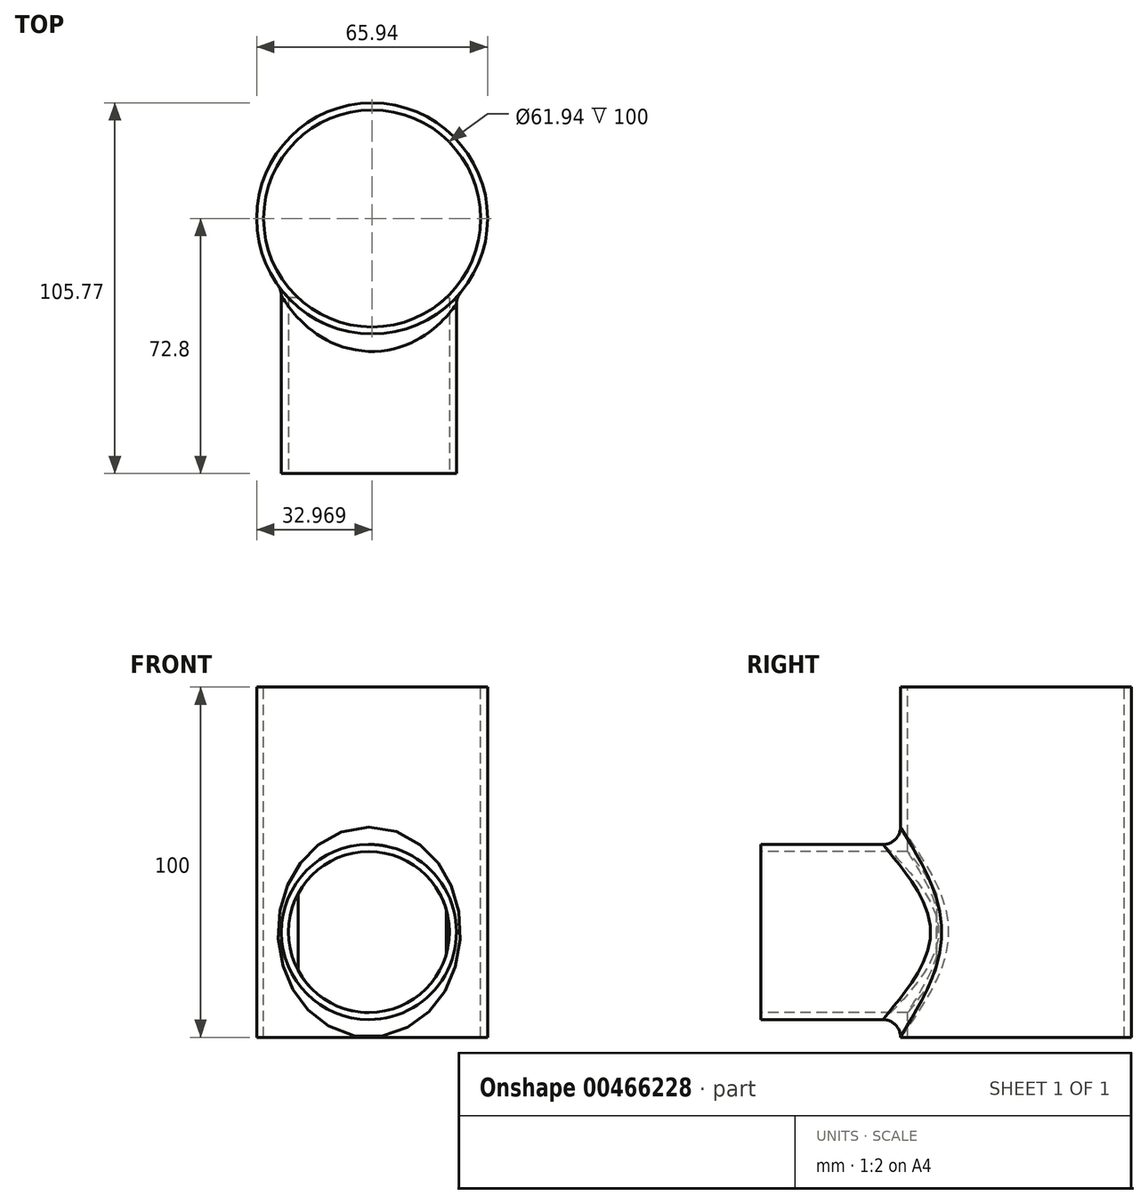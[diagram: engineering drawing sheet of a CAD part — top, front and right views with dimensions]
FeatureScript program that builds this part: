
annotation { "Feature Type Name" : "Feature", "Feature Type Description" : "" }
export const myFeature = defineFeature(function(context is Context, id is Id, definition is map)
    precondition{}
    {
        {
            var Q0;
            Q0=qCreatedBy(makeId("Top.planeOp"),FACE);
            var sketch = newSketch(context, id + "F0", { "sketchPlane" : qUnion([Q0])});
            skCircle(sketch, "E0", {"center": v(35.44, 0) * mm, "radius": 32.97 * mm});
            skSolve(sketch);
        }
        {
            var Q0;
            Q0=makeQuery(id+"F0.imprint","IMPRINT",FACE,{"disambiguationData":[TD([[makeQuery(id+"F0.imprint","IMPRINT",EDGE,{"derivedFrom":sQuery(id+"F0.wireOp",EDGE,"E0")}),1.0]])]});
            extrude(context, id + "F1", {"entities" : qUnion([Q0]), "depth" : 100 * mm, "offsetDistance" : 25 * mm});
        }
        {
            var Q0;
            Q0=makeQuery(id+"F1.opExtrude","CAP_FACE",FACE,{"disambiguationData":[OSD([sQuery(id+"F0.wireOp",EDGE,"E0")])],"isStart":false});
            var sketch = newSketch(context, id + "F2", { "sketchPlane" : qUnion([Q0])});
            skCircle(sketch, "E1.0", {"center": v(35.44, 0) * mm, "radius": 30.97 * mm});
            skSolve(sketch);
        }
        {
            var Q0;
            Q0=makeQuery(id+"F2.imprint","IMPRINT",FACE,{"disambiguationData":[TD([[makeQuery(id+"F2.imprint","IMPRINT",EDGE,{"derivedFrom":sQuery(id+"F2.wireOp",EDGE,"E1.0")}),1.0]])]});
            extrude(context, id + "F3", {"entities" : qUnion([Q0]), "operationType" : NewBodyOperationType.REMOVE, "oppositeDirection" : true, "depth" : 100 * mm, "offsetDistance" : 25 * mm});
        }
        {
            var Q0;
            Q0=qCreatedBy(makeId("Front.planeOp"),FACE);
            var sketch = newSketch(context, id + "F4", { "sketchPlane" : qUnion([Q0])});
            skCircle(sketch, "E2", {"center": v(34.52, 30.05) * mm, "radius": 25 * mm});
            skSolve(sketch);
        }
        {
            var Q0;
            Q0=makeQuery(id+"F4.imprint","IMPRINT",FACE,{"disambiguationData":[TD([[makeQuery(id+"F4.imprint","IMPRINT",EDGE,{"derivedFrom":sQuery(id+"F4.wireOp",EDGE,"E2")}),1.0]])]});
            var Q1;
            Q1=sQuery(id+"F4.wireOp",EDGE,"E2");
            extrude(context, id + "F5", {"entities" : qUnion([Q0]), "operationType" : NewBodyOperationType.ADD, "surfaceEntities" : qUnion([Q1]), "depth" : 72.8 * mm, "offsetDistance" : 25 * mm});
        }
        {
            var Q0;
            Q0=makeQuery(id+"F5.boolean.opBoolean","INTERSECT",EDGE,{"derivedFrom":[makeQuery(id+"F1.opExtrude","SWEPT_FACE",FACE,{"disambiguationData":[OSD([sQuery(id+"F0.wireOp",EDGE,"E0")])]}),makeQuery(id+"F5.opExtrude","SWEPT_FACE",FACE,{"disambiguationData":[OSD([sQuery(id+"F4.wireOp",EDGE,"E2")])]})]});
            fillet(context, id + "F6", {"entities" : qUnion([Q0]), "radius" : 5 * mm, "tangentPropagation" : true, "allowEdgeOverflow" : false});
        }
        {
            var Q0;
            Q0=makeQuery(id+"F5.opExtrude","CAP_FACE",FACE,{"disambiguationData":[OSD([sQuery(id+"F4.wireOp",EDGE,"E2")])],"isStart":false});
            var sketch = newSketch(context, id + "F7", { "sketchPlane" : qUnion([Q0])});
            skCircle(sketch, "E3.0", {"center": v(34.52, 30.05) * mm, "radius": 23 * mm});
            skSolve(sketch);
        }
        {
            var Q0;
            Q0 = qSketchRegion(id + "F7", true);
            extrude(context, id + "F8", {"entities" : qUnion([Q0]), "operationType" : NewBodyOperationType.REMOVE, "oppositeDirection" : true, "depth" : 50.18 * mm, "offsetDistance" : 25 * mm});
        }
        {
            var Q0;
            Q0=makeQuery(id+"F1.opExtrude","CAP_FACE",FACE,{"disambiguationData":[OSD([sQuery(id+"F0.wireOp",EDGE,"E0")])],"isStart":false});
            var sketch = newSketch(context, id + "F9", { "sketchPlane" : qUnion([Q0])});
            skCircle(sketch, "E4.0", {"center": v(35.44, 0) * mm, "radius": 30.97 * mm});
            skSolve(sketch);
        }
        {
            var Q0;
            Q0 = qSketchRegion(id + "F9", true);
            extrude(context, id + "F10", {"entities" : qUnion([Q0]), "operationType" : NewBodyOperationType.REMOVE, "oppositeDirection" : true, "depth" : 126.6 * mm, "offsetDistance" : 25 * mm});
        }
    });
